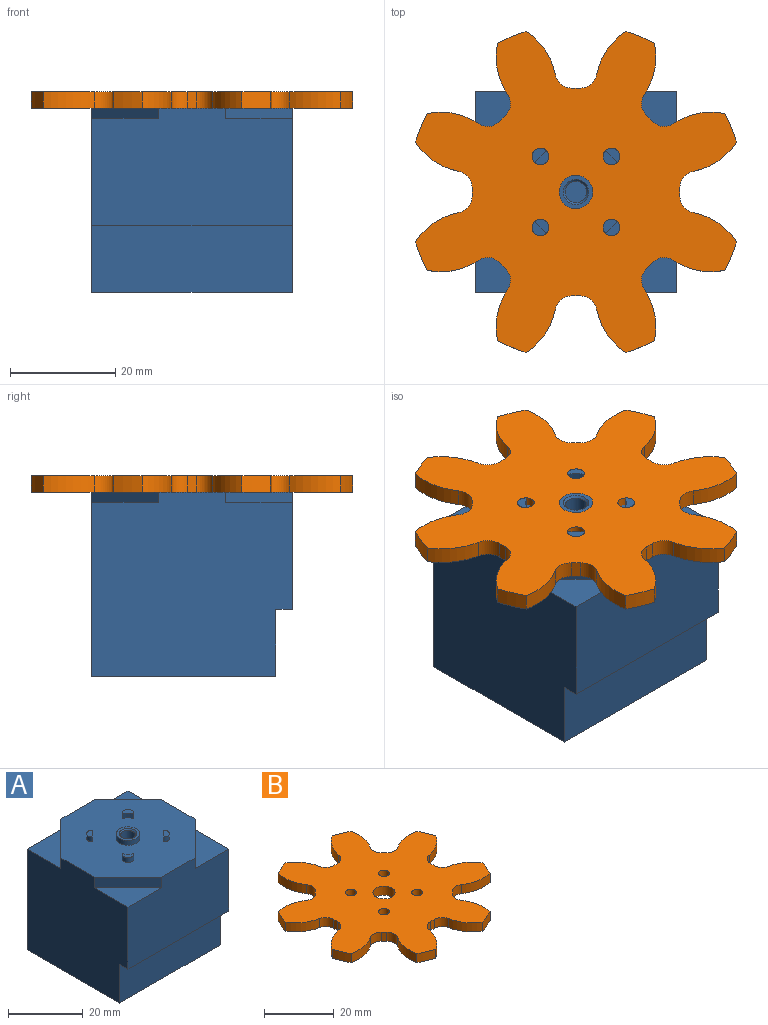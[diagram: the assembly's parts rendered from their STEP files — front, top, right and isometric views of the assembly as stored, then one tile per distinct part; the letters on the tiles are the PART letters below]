
ASSEMBLY  parts=2 mates=1
PART A: 33 faces, bbox 38.1x38.1x38.1 mm
  f0: cylinder r=1.59mm len=2.8mm, axis (0,0,-1), area 8.4mm2, adj f9,f12,f31
  f1: cylinder r=1.59mm len=2.8mm, axis (0,0,-1), area 8.4mm2, adj f9,f13,f30
  f2: cylinder r=1.59mm len=2.8mm, axis (0,0,-1), area 8.4mm2, adj f9,f14,f29
  f3: cylinder r=1.59mm len=2.8mm, axis (0,0,-1), area 8.4mm2, adj f9,f15,f28
  f4: plane 38.1x36.5mm, normal (-1,0,0), area 1261.9mm2, adj f5,f6,f8,f9,f17,f20,f21,f24
  f5: plane 38.1x34.93mm, normal (0,0,-1), area 1330.6mm2, adj f4,f7,f8,f26
  f6: plane 38.1x23.8mm, normal (0,-1,0), area 818.4mm2, adj f4,f7,f9,f19,f20,f21,f22,f27
  f7: plane 38.1x36.5mm, normal (1,0,0), area 1261.9mm2, adj f5,f6,f8,f9,f18,f19,f22,f23
  f8: plane 38.1x36.5mm, normal (0,1,0), area 1302.3mm2, adj f4,f5,f7,f9,f17,f18,f23,f24
  f9: plane 38.1x38.1mm, normal (0,0,1), area 1081mm2, adj f0,f1,f2,f3,f4,f6,f7,f8
  f10: cylinder r=3.17mm len=6.35mm, axis (0,0,-1), area 31.9mm2, adj f9,f11
  f11: plane 6.35x6.35mm, normal (0,0,1), area 13.6mm2, adj f10,f32
  f12: plane 2.8x2.8mm, normal (0,0,1), area 4.1mm2, adj f0,f31
  f13: plane 2.8x2.8mm, normal (0,0,1), area 4.1mm2, adj f1,f30
  f14: plane 2.8x2.8mm, normal (0,0,1), area 4.1mm2, adj f2,f29
  f15: plane 2.8x2.8mm, normal (0,0,1), area 4.1mm2, adj f3,f28
  f16: cylinder r=2.02mm len=4.7mm, axis (0,0,1), area 59.6mm2, adj f25,f32
  f17: plane 12.7x12.7mm, normal (-0.71,0.71,0), area 62.5mm2, adj f4,f8,f9,f24
  f18: plane 12.7x12.7mm, normal (0.71,0.71,0), area 62.5mm2, adj f7,f8,f9,f23
  f19: plane 12.7x12.7mm, normal (0.71,-0.71,0), area 62.5mm2, adj f6,f7,f9,f22
  f20: plane 12.7x12.7mm, normal (-0.71,-0.71,0), area 62.5mm2, adj f4,f6,f9,f21
  f21: plane 12.7x12.7mm, normal (0,0,1), area 80.6mm2, adj f4,f6,f20
  f22: plane 12.7x12.7mm, normal (0,0,1), area 80.6mm2, adj f6,f7,f19
  f23: plane 12.7x12.7mm, normal (0,0,1), area 80.6mm2, adj f7,f8,f18
  f24: plane 12.7x12.7mm, normal (0,0,1), area 80.6mm2, adj f4,f8,f17
  f25: plane 4.04x4.04mm, normal (0,0,1), area 12.8mm2, adj f16
  f26: plane 38.1x12.7mm, normal (0,-1,0), area 483.9mm2, adj f4,f5,f7,f27
  f27: plane 38.1x3.18mm, normal (0,0,-1), area 121mm2, adj f4,f6,f7,f26
  f28: cylinder r=9.53mm len=2.24mm, axis (0,0,-1), area 5.1mm2, adj f3,f9,f15
  f29: cylinder r=9.53mm len=2.24mm, axis (0,0,-1), area 5.1mm2, adj f2,f9,f14
  f30: cylinder r=9.53mm len=2.24mm, axis (0,0,-1), area 5.1mm2, adj f1,f9,f13
  f31: cylinder r=9.53mm len=2.24mm, axis (0,0,-1), area 5.1mm2, adj f0,f9,f12
  f32: cone r=2.02mm half-angle=45deg, axis (0,0,1), area 7.5mm2, adj f11,f16
PART B: 55 faces, bbox 60.9x60.9x3.2 mm
  f0: plane 60.94x60.94mm, normal (0,0,1), area 2090mm2, adj f2,f3,f4,f5,f6,f7,f8,f9
  f1: plane 60.94x60.94mm, normal (0,0,-1), area 2090mm2, adj f2,f3,f4,f5,f6,f7,f8,f9
  f2: cylinder r=31.9mm len=5.4mm, axis (0,0,-1), area 18.6mm2, adj f0,f1,f6,f45
  f3: plane 3.18x1.13mm, normal (0.71,0.71,0), area 5.1mm2, adj f0,f1,f4,f7
  f4: cylinder r=3.17mm len=4.01mm, axis (0,0,-1), area 13.9mm2, adj f0,f1,f3,f5
  f5: cylinder r=12.7mm len=9.72mm, axis (0,0,-1), area 32.3mm2, adj f0,f1,f4,f8
  f6: cylinder r=12.7mm len=9.72mm, axis (0,0,-1), area 32.3mm2, adj f0,f1,f2,f7
  f7: cylinder r=3.17mm len=4.01mm, axis (0,0,-1), area 13.9mm2, adj f0,f1,f3,f6
  f8: cylinder r=31.9mm len=5.4mm, axis (0,0,-1), area 18.6mm2, adj f0,f1,f5,f12
  f9: plane 3.18x1.6mm, normal (1,0,0), area 5.1mm2, adj f0,f1,f10,f13
  f10: cylinder r=3.17mm len=3.18mm, axis (0,0,-1), area 13.9mm2, adj f0,f1,f9,f11
  f11: cylinder r=12.7mm len=8.2mm, axis (0,0,-1), area 32.3mm2, adj f0,f1,f10,f14
  f12: cylinder r=12.7mm len=8.2mm, axis (0,0,-1), area 32.3mm2, adj f0,f1,f8,f13
  f13: cylinder r=3.17mm len=3.18mm, axis (0,0,-1), area 13.9mm2, adj f0,f1,f9,f12
  f14: cylinder r=31.9mm len=5.4mm, axis (0,0,-1), area 18.6mm2, adj f0,f1,f11,f18
  f15: plane 3.18x1.13mm, normal (0.71,-0.71,0), area 5.1mm2, adj f0,f1,f16,f19
  f16: cylinder r=3.17mm len=4.01mm, axis (0,0,-1), area 13.9mm2, adj f0,f1,f15,f17
  f17: cylinder r=12.7mm len=9.72mm, axis (0,0,-1), area 32.3mm2, adj f0,f1,f16,f20
  f18: cylinder r=12.7mm len=9.72mm, axis (0,0,-1), area 32.3mm2, adj f0,f1,f14,f19
  f19: cylinder r=3.17mm len=4.01mm, axis (0,0,-1), area 13.9mm2, adj f0,f1,f15,f18
  f20: cylinder r=31.9mm len=5.4mm, axis (0,0,-1), area 18.6mm2, adj f0,f1,f17,f24
  f21: plane 3.18x1.6mm, normal (0,-1,0), area 5.1mm2, adj f0,f1,f22,f25
  f22: cylinder r=3.17mm len=3.18mm, axis (0,0,-1), area 13.9mm2, adj f0,f1,f21,f23
  f23: cylinder r=12.7mm len=8.2mm, axis (0,0,-1), area 32.3mm2, adj f0,f1,f22,f26
  f24: cylinder r=12.7mm len=8.2mm, axis (0,0,-1), area 32.3mm2, adj f0,f1,f20,f25
  f25: cylinder r=3.17mm len=3.18mm, axis (0,0,-1), area 13.9mm2, adj f0,f1,f21,f24
  f26: cylinder r=31.9mm len=5.4mm, axis (0,0,-1), area 18.6mm2, adj f0,f1,f23,f30
  f27: plane 3.18x1.13mm, normal (-0.71,-0.71,0), area 5.1mm2, adj f0,f1,f28,f31
  f28: cylinder r=3.17mm len=4.01mm, axis (0,0,-1), area 13.9mm2, adj f0,f1,f27,f29
  f29: cylinder r=12.7mm len=9.72mm, axis (0,0,-1), area 32.3mm2, adj f0,f1,f28,f32
  f30: cylinder r=12.7mm len=9.72mm, axis (0,0,-1), area 32.3mm2, adj f0,f1,f26,f31
  f31: cylinder r=3.17mm len=4.01mm, axis (0,0,-1), area 13.9mm2, adj f0,f1,f27,f30
  f32: cylinder r=31.9mm len=5.4mm, axis (0,0,-1), area 18.6mm2, adj f0,f1,f29,f36
  f33: plane 3.18x1.6mm, normal (-1,0,0), area 5.1mm2, adj f0,f1,f34,f37
  f34: cylinder r=3.17mm len=3.18mm, axis (0,0,-1), area 13.9mm2, adj f0,f1,f33,f35
  f35: cylinder r=12.7mm len=8.2mm, axis (0,0,-1), area 32.3mm2, adj f0,f1,f34,f38
  f36: cylinder r=12.7mm len=8.2mm, axis (0,0,-1), area 32.3mm2, adj f0,f1,f32,f37
  f37: cylinder r=3.17mm len=3.18mm, axis (0,0,-1), area 13.9mm2, adj f0,f1,f33,f36
  f38: cylinder r=31.9mm len=5.4mm, axis (0,0,-1), area 18.6mm2, adj f0,f1,f35,f42
  f39: plane 3.18x1.13mm, normal (-0.71,0.71,0), area 5.1mm2, adj f0,f1,f40,f43
  f40: cylinder r=3.17mm len=4.01mm, axis (0,0,-1), area 13.9mm2, adj f0,f1,f39,f41
  f41: cylinder r=12.7mm len=9.72mm, axis (0,0,-1), area 32.3mm2, adj f0,f1,f40,f44
  f42: cylinder r=12.7mm len=9.72mm, axis (0,0,-1), area 32.3mm2, adj f0,f1,f38,f43
  f43: cylinder r=3.17mm len=4.01mm, axis (0,0,-1), area 13.9mm2, adj f0,f1,f39,f42
  f44: cylinder r=31.9mm len=5.4mm, axis (0,0,-1), area 18.6mm2, adj f0,f1,f41,f46
  f45: cylinder r=12.7mm len=8.2mm, axis (0,0,-1), area 32.3mm2, adj f0,f1,f2,f48
  f46: cylinder r=12.7mm len=8.2mm, axis (0,0,-1), area 32.3mm2, adj f0,f1,f44,f49
  f47: plane 3.18x1.6mm, normal (0,1,0), area 5.1mm2, adj f0,f1,f48,f49
  f48: cylinder r=3.17mm len=3.18mm, axis (0,0,-1), area 13.9mm2, adj f0,f1,f45,f47
  f49: cylinder r=3.17mm len=3.18mm, axis (0,0,-1), area 13.9mm2, adj f0,f1,f46,f47
  f50: cylinder r=3.17mm len=6.35mm, axis (0,0,1), area 63.3mm2, adj f0,f1
  f51: cylinder r=1.59mm len=3.18mm, axis (0,0,-1), area 31.7mm2, adj f0,f1
  f52: cylinder r=1.59mm len=3.18mm, axis (0,0,-1), area 31.7mm2, adj f0,f1
  f53: cylinder r=1.59mm len=3.18mm, axis (0,0,-1), area 31.7mm2, adj f0,f1
  f54: cylinder r=1.59mm len=3.18mm, axis (0,0,-1), area 31.7mm2, adj f0,f1
PLACE A t=(9.5,19.94,1.49)mm
PLACE B rot(axis=(1,0,0),180deg) t=(9.5,19.94,39.59)mm
MATE fastened B.f50 <-> A.f16  axis (0,0,1) through (9.5,19.94,39.59)mm
